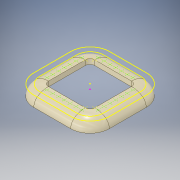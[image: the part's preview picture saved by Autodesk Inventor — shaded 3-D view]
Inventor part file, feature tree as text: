
AUTODESK INVENTOR PART (.ipt)
format: ipt  version: 2018 (Build 220112000, 112)  size: 677,376 bytes
history: native  units: in
note: dims shown in document units (in); Inventor stores cm internally (conversion verified against a paired STEP export)
features: projected_geometry x9, other x8, thicken_offset x3, plane x3, extrude x2, sketch x2, split x1, delete_face x1
ambient origin geometry x8: Origin, YZ Plane, XZ Plane, XY Plane, X Axis, Y Axis, Z Axis, Center Point
bodies: Solid3 (feature_tree), Solid1 (feature_tree)
feature tree (29):
  other  "Remote Shell.ipt"
  thicken_offset  "Thicken1"
  thicken_offset  "Thicken2"
  split  "Split1"
  extrude  "Extrusion7"  Depth=0.12in
  plane  "Work Plane13"
  extrude  "Extrusion16"  Depth=0.16in
  thicken_offset  "Thicken7"
  plane  "Work Plane7"
  plane  "Work Plane18"
  other  "New peg sketch"
  other  "Alignment Sketch"
  other  "3/16" Vacuum Drill Sketch"
  delete_face  "Delete Face1"
  other  "Top Solid::Remote Shell.ipt"
  other  "TaggingFeature1"
  other  "Srf1"
  sketch  "Sketch9"  dims[d0=0.3937in d1=0.12in d2=0.1in]
  sketch  "Sketch19"  dims[d57=0.0375in d58=0.02in d63=0.16in d64=0.0in d65=0.0in d148=0.125in d149=0.125in d150=0.125in d151=0.125in d152=0.125in d153=1.0in d154=0.0in d157=0.015in d158=0.015in d299=0.1in d300=0.1in d301=0.1in d302=0.1in d303=2.7559in d305=0.1562in d306=0.3937in d308=1.0in d310=2.7559in d312=0.1562in d313=0.3937in d315=1.0in d317=2.7559in d319=0.1562in d320=0.3937in d322=1.0in d324=2.7559in d326=0.1562in d327=0.3937in d329=1.0in d333=0.25in]
  projected_geometry  "Projected Loop39"
  projected_geometry  "Projected Loop40"
  projected_geometry  "Projected Loop41"
  projected_geometry  "Projected Loop42"
  projected_geometry  "Projected Loop43"
  projected_geometry  "Projected Loop44"
  projected_geometry  "Projected Loop45"
  projected_geometry  "Projected Loop46"
  projected_geometry  "Projected Loop47"
  other  "Srf1::Derived"
